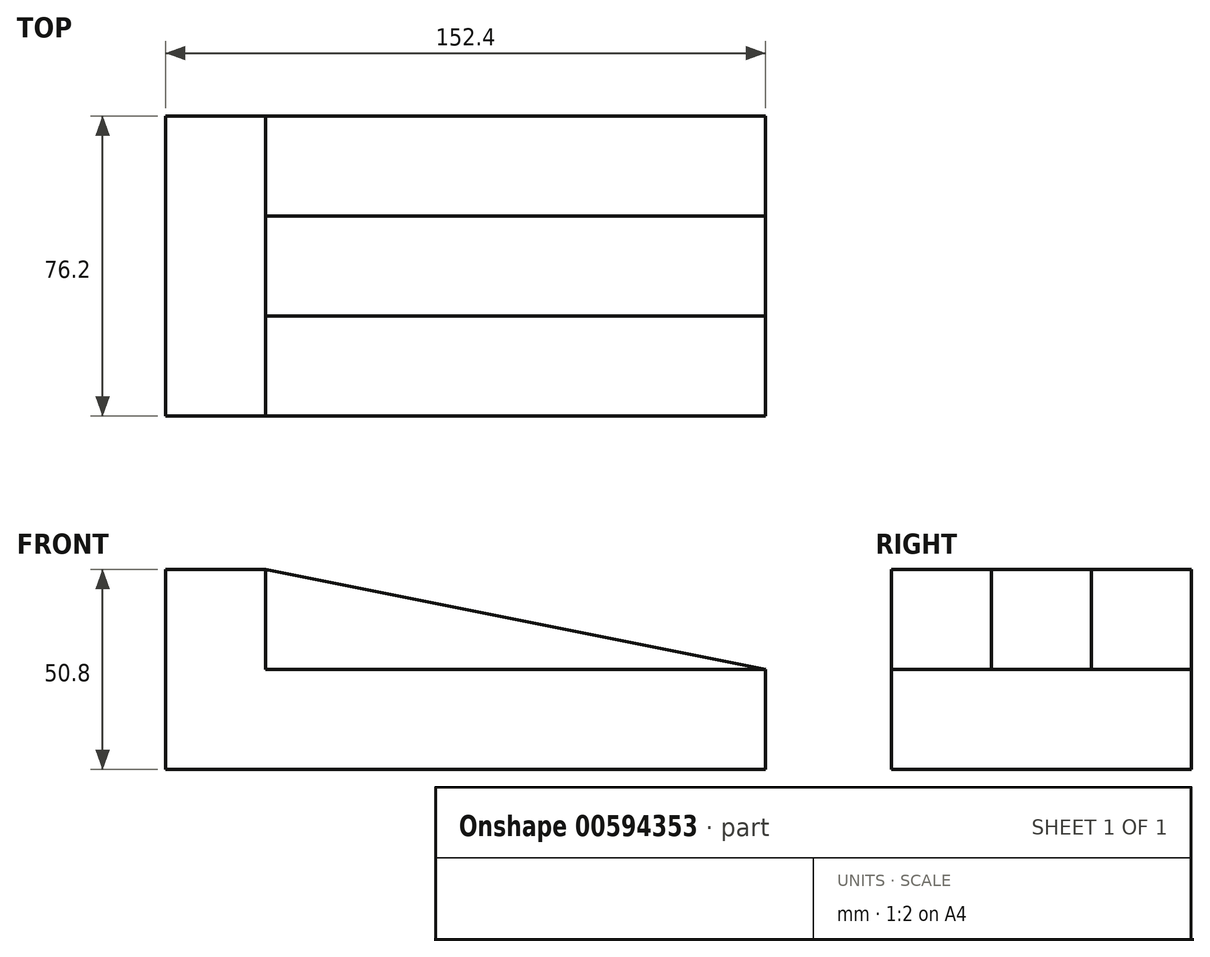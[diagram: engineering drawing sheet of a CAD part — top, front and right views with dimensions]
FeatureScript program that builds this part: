
annotation { "Feature Type Name" : "Feature", "Feature Type Description" : "" }
export const myFeature = defineFeature(function(context is Context, id is Id, definition is map)
    precondition{}
    {
        {
            var Q0;
            Q0=qCreatedBy(makeId("Front.planeOp"),FACE);
            var sketch = newSketch(context, id + "F0", { "sketchPlane" : qUnion([Q0])});
            skLineSegment(sketch, "E0.bottom", {"start": v(0, 0) * mm, "end": v(152.4, 0) * mm});
            skLineSegment(sketch, "E0.top", {"start": v(0, 50.8) * mm, "end": v(152.4, 50.8) * mm});
            skLineSegment(sketch, "E0.left", {"start": v(0, 0) * mm, "end": v(0, 50.8) * mm});
            skLineSegment(sketch, "E0.right", {"start": v(152.4, 0) * mm, "end": v(152.4, 50.8) * mm});
            skSolve(sketch);
        }
        {
            var Q0;
            Q0=makeQuery(id+"F0.imprint","IMPRINT",FACE,{"disambiguationData":[TD([[makeQuery(id+"F0.imprint","IMPRINT",EDGE,{"derivedFrom":sQuery(id+"F0.wireOp",EDGE,"E0.bottom")}),1.0]])]});
            extrude(context, id + "F1", {"entities" : qUnion([Q0]), "oppositeDirection" : true, "depth" : 76.2 * mm, "offsetDistance" : 25.4 * mm});
        }
        {
            var Q0;
            Q0=makeQuery(id+"F1.opExtrude","SWEPT_FACE",FACE,{"disambiguationData":[OSD([sQuery(id+"F0.wireOp",EDGE,"E0.top")])]});
            var sketch = newSketch(context, id + "F2", { "sketchPlane" : qUnion([Q0])});
            skLineSegment(sketch, "E1", {"start": v(152.4, 0) * mm, "end": v(152.4, 25.4) * mm});
            skLineSegment(sketch, "E2", {"start": v(152.4, 25.4) * mm, "end": v(25.4, 25.4) * mm});
            skLineSegment(sketch, "E3", {"start": v(25.4, 25.4) * mm, "end": v(25.4, 0) * mm});
            skLineSegment(sketch, "E4", {"start": v(25.4, 0) * mm, "end": v(152.4, 0) * mm});
            skSolve(sketch);
        }
        {
            var Q0;
            Q0=makeQuery(id+"F2.imprint","IMPRINT",FACE,{"disambiguationData":[TD([[makeQuery(id+"F2.imprint","IMPRINT",EDGE,{"derivedFrom":sQuery(id+"F2.wireOp",EDGE,"E1")}),-1.0]])]});
            extrude(context, id + "F3", {"entities" : qUnion([Q0]), "operationType" : NewBodyOperationType.REMOVE, "oppositeDirection" : true, "depth" : 25.4 * mm, "offsetDistance" : 25.4 * mm});
        }
        {
            var Q0;
            Q0=makeQuery(id+"F1.opExtrude","SWEPT_FACE",FACE,{"disambiguationData":[OSD([sQuery(id+"F0.wireOp",EDGE,"E0.top")])]});
            var sketch = newSketch(context, id + "F4", { "sketchPlane" : qUnion([Q0])});
            skLineSegment(sketch, "E5", {"start": v(152.4, 76.2) * mm, "end": v(25.4, 76.2) * mm});
            skLineSegment(sketch, "E6", {"start": v(25.4, 76.2) * mm, "end": v(25.4, 50.8) * mm});
            skLineSegment(sketch, "E7", {"start": v(25.4, 50.8) * mm, "end": v(152.4, 50.8) * mm});
            skLineSegment(sketch, "E8", {"start": v(152.4, 50.8) * mm, "end": v(152.4, 76.2) * mm});
            skSolve(sketch);
        }
        {
            var Q0;
            Q0=makeQuery(id+"F4.imprint","IMPRINT",FACE,{"disambiguationData":[TD([[makeQuery(id+"F4.imprint","IMPRINT",EDGE,{"derivedFrom":sQuery(id+"F4.wireOp",EDGE,"E5")}),-1.0]])]});
            extrude(context, id + "F5", {"entities" : qUnion([Q0]), "operationType" : NewBodyOperationType.REMOVE, "oppositeDirection" : true, "depth" : 25.4 * mm, "offsetDistance" : 25.4 * mm});
        }
        {
            var Q0;
            Q0=makeQuery(id+"F3.boolean.opBoolean","COPY",FACE,{"derivedFrom":makeQuery(id+"F3.opExtrude","SWEPT_FACE",FACE,{"disambiguationData":[OSD([sQuery(id+"F2.wireOp",EDGE,"E2")])]})});
            var sketch = newSketch(context, id + "F6", { "sketchPlane" : qUnion([Q0])});
            skLineSegment(sketch, "E9", {"start": v(25.4, 50.8) * mm, "end": v(152.4, 25.4) * mm});
            skLineSegment(sketch, "E10", {"start": v(152.4, 25.4) * mm, "end": v(152.4, 50.8) * mm});
            skLineSegment(sketch, "E11", {"start": v(152.4, 50.8) * mm, "end": v(25.4, 50.8) * mm});
            skSolve(sketch);
        }
        {
            var Q0;
            Q0=makeQuery(id+"F6.imprint","IMPRINT",FACE,{"disambiguationData":[TD([[makeQuery(id+"F6.imprint","IMPRINT",EDGE,{"derivedFrom":sQuery(id+"F6.wireOp",EDGE,"E9")}),1.0]])]});
            extrude(context, id + "F7", {"entities" : qUnion([Q0]), "operationType" : NewBodyOperationType.REMOVE, "oppositeDirection" : true, "depth" : 25.4 * mm, "offsetDistance" : 25.4 * mm});
        }
    });
